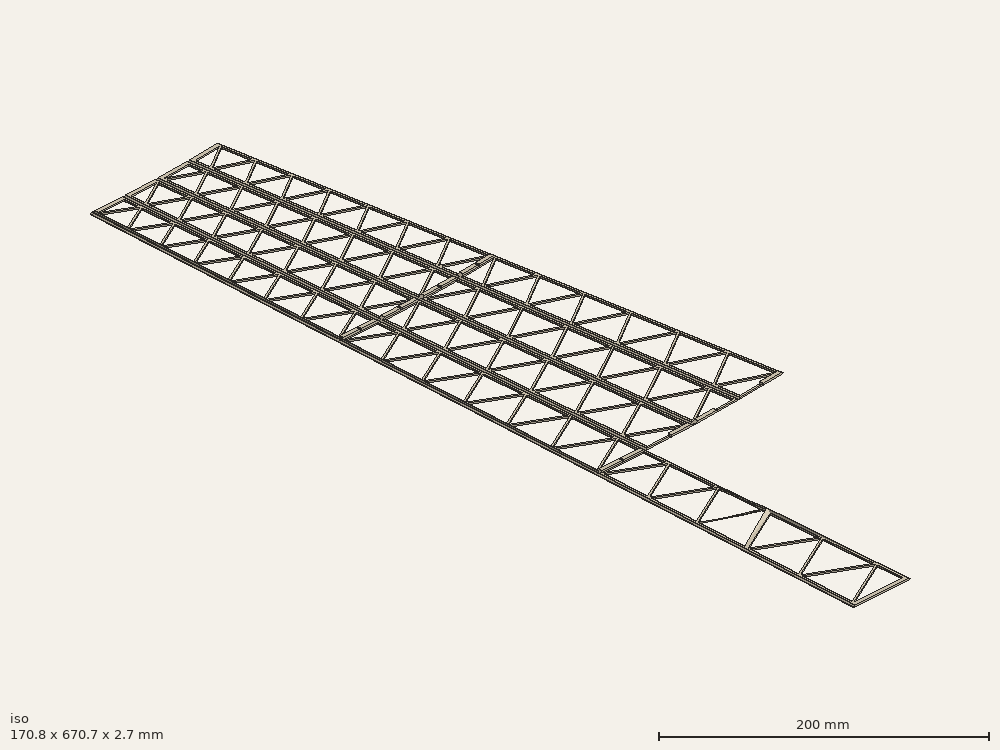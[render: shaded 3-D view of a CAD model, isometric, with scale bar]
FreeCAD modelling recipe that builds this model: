
FCSTD DOCUMENT  (FreeCAD 1.0R39319 (Git))
Label: DSB_30m_lystaarn_2
License: All rights reserved
LicenseURL: http://en.wikipedia.org/wiki/All_rights_reserved
objects: Sketcher::SketchObject×15, PartDesign::AdditivePipe×6, PartDesign::Body×4, PartDesign::Mirrored×4, PartDesign::SubShapeBinder×3, PartDesign::Pad×3, PartDesign::Chamfer×3, Image::ImagePlane×1, App::VarSet×1
note: 81 computed .brp shape members not serialized (recipe doc carries the construction recipe); baked Part::Feature solids carry a one-line shape summary decoded from their .brp

FEATURE [Image::ImagePlane] Taarn
  Placement = pos=(-63.4214,156.887,0) rot=(0,0,1;0.012217rad)
  XSize = 407.33
  YSize = 576.174
FEATURE [App::VarSet] VarSet
  IronLegWidth = 3
  IronSupportWidth = 1.5
  TowerBottomWidth = 45.5
  TowerHeight = 662.6
  TowerTopWidth = 25.97
  expr: TowerHeight = 353.87 + 308.73
FEATURE [Sketcher::SketchObject] Sketch  label="Basic Measurements"
  ArcFitTolerance = 1e-06
  AttachmentSupport = -> [XY_Plane]
  FullyConstrained = false
  MakeInternals = false
  MapMode = 5
  sketch-geometry (6):
    g0: LineSegment StartX=-22.75 StartY=0 StartZ=0 EndX=22.75 EndY=0 EndZ=0
    g1: LineSegment StartX=0 StartY=0 StartZ=0 EndX=0 EndY=353.87 EndZ=0
    g2: LineSegment StartX=-157.614 StartY=302.942 StartZ=0 EndX=-131.644 EndY=302.942 EndZ=0
    g3: LineSegment StartX=-144.629 StartY=302.942 StartZ=0 EndX=-143.643 EndY=-5.78841 EndZ=0
    g4: LineSegment StartX=-96.211 StartY=303.16 StartZ=0 EndX=-48.4821 EndY=303.16 EndZ=0
    g5: LineSegment StartX=-48.4821 StartY=327.388 StartZ=0 EndX=-48.4821 EndY=303.16 EndZ=0
  constraints (14):
    c: PointOnObject(g0,g-1)
    c: Coincident(g1,g-1)
    c: Vertical(g1)
    c: Symmetric(g0,g0,g1)
    c: DistanceX(g0,g0) = 45.5
    c: Horizontal(g2)
    c: DistanceX(g2,g2) = 25.97
    c: Symmetric(g2,g2,g3)
    c: DistanceY(g3,g3) = 308.73
    c: DistanceY(g1,g1) = 353.87
    c: Horizontal(g4)
    c: DistanceX(g4,g4) = 47.7289
    c: Coincident(g5,g4)
    c: DistanceY(g5,g5) = 24.2284
FEATURE [Sketcher::SketchObject] Sketch001  label="Basic Lattice Mast"
  ArcFitTolerance = 1e-06
  AttachmentSupport = -> [XY_Plane]
  FullyConstrained = true
  MakeInternals = false
  MapMode = 5
  expr: Constraints[128] = VarSet.IronSupportWidth
  expr: Constraints[56] = VarSet.IronSupportWidth * 2
  expr: Constraints[7] = VarSet.TowerTopWidth
  expr: Constraints[8] = VarSet.TowerBottomWidth
  expr: Constraints[91] = VarSet.IronSupportWidth * 2
  expr: Constraints[9] = VarSet.TowerHeight
  sketch-geometry (45):
    g0: LineSegment StartX=-22.75 StartY=0 StartZ=0 EndX=-12.985 EndY=662.6 EndZ=0
    g1: LineSegment StartX=-12.985 StartY=662.6 StartZ=0 EndX=12.985 EndY=662.6 EndZ=0
    g2: LineSegment StartX=12.985 StartY=662.6 StartZ=0 EndX=22.75 EndY=0 EndZ=0
    g3: LineSegment StartX=22.75 StartY=0 StartZ=0 EndX=-22.75 EndY=0 EndZ=0
    g4: LineSegment StartX=-22.7279 StartY=1.5 StartZ=0 EndX=22.3814 EndY=25.0125 EndZ=0
    g5: LineSegment StartX=22.3814 StartY=25.0125 StartZ=0 EndX=-22.0402 EndY=48.1665 EndZ=0
    g6: LineSegment StartX=-22.0402 StartY=48.1665 StartZ=0 EndX=21.7041 EndY=70.9675 EndZ=0
    g7: LineSegment StartX=21.7041 StartY=70.9675 StartZ=0 EndX=-21.3732 EndY=93.4209 EndZ=0
    g8: LineSegment [constr] StartX=22.3814 StartY=25.0125 StartZ=0 EndX=-22.3814 EndY=25.0125 EndZ=0
    g9: ArcOfCircle [constr] CenterX=22.3814 CenterY=25.0125 CenterZ=0 NormalX=0 NormalY=0 NormalZ=1 AngleXU=0 Radius=30 StartAngle=2.6611 EndAngle=3.62208
    g10: LineSegment [constr] StartX=-4.22167 StartY=38.8789 StartZ=0 EndX=-4.22167 EndY=11.1461 EndZ=0
    g11: LineSegment StartX=-21.3732 StartY=93.4209 StartZ=0 EndX=21.0474 EndY=115.532 EndZ=0
    g12: LineSegment StartX=21.0474 StartY=115.532 StartZ=0 EndX=-20.7265 EndY=137.306 EndZ=0
    g13: LineSegment StartX=-20.7265 StartY=137.306 StartZ=0 EndX=20.4105 EndY=158.748 EndZ=0
    g14: LineSegment StartX=20.4105 StartY=158.748 StartZ=0 EndX=-20.0993 EndY=179.863 EndZ=0
    g15: LineSegment StartX=-20.0993 StartY=179.863 StartZ=0 EndX=19.7929 EndY=200.656 EndZ=0
    g16: LineSegment StartX=19.7929 StartY=200.656 StartZ=0 EndX=-19.4911 EndY=221.132 EndZ=0
    g17: LineSegment StartX=-19.4469 StartY=224.132 StartZ=0 EndX=19.1504 EndY=244.25 EndZ=0
    g18: LineSegment StartX=19.1504 StartY=244.25 StartZ=0 EndX=-18.8584 EndY=264.062 EndZ=0
    g19: LineSegment StartX=-18.8584 StartY=264.062 StartZ=0 EndX=18.5709 EndY=283.571 EndZ=0
    g20: LineSegment StartX=18.5709 StartY=283.571 StartZ=0 EndX=-18.2878 EndY=302.783 EndZ=0
    g21: LineSegment StartX=-18.2878 StartY=302.783 StartZ=0 EndX=18.0089 EndY=321.702 EndZ=0
    g22: LineSegment StartX=18.0089 StartY=321.702 StartZ=0 EndX=-17.7344 EndY=340.333 EndZ=0
    g23: LineSegment StartX=-17.7344 StartY=340.333 StartZ=0 EndX=17.464 EndY=358.68 EndZ=0
    g24: LineSegment StartX=17.464 StartY=358.68 StartZ=0 EndX=-17.1977 EndY=376.747 EndZ=0
    g25: LineSegment StartX=-17.1977 StartY=376.747 StartZ=0 EndX=16.9355 EndY=394.538 EndZ=0
    g26: LineSegment StartX=16.9355 StartY=394.538 StartZ=0 EndX=-16.6773 EndY=412.058 EndZ=0
    g27: LineSegment StartX=-16.6773 StartY=412.058 StartZ=0 EndX=16.4231 EndY=429.311 EndZ=0
    g28: LineSegment StartX=16.4231 StartY=429.311 StartZ=0 EndX=-16.1727 EndY=446.301 EndZ=0
    g29: LineSegment StartX=-16.1285 StartY=449.301 StartZ=0 EndX=15.8826 EndY=465.987 EndZ=0
    g30: LineSegment StartX=15.8826 StartY=465.987 StartZ=0 EndX=-15.6404 EndY=482.417 EndZ=0
    g31: LineSegment StartX=-15.6404 StartY=482.417 StartZ=0 EndX=15.402 EndY=498.598 EndZ=0
    g32: LineSegment StartX=15.402 StartY=498.598 StartZ=0 EndX=-15.1671 EndY=514.531 EndZ=0
    g33: LineSegment StartX=-15.1671 StartY=514.531 StartZ=0 EndX=14.9359 EndY=530.222 EndZ=0
    g34: LineSegment StartX=14.9359 StartY=530.222 StartZ=0 EndX=-14.7082 EndY=545.674 EndZ=0
    g35: LineSegment StartX=-14.7082 StartY=545.674 StartZ=0 EndX=14.4839 EndY=560.89 EndZ=0
    g36: LineSegment StartX=14.4839 StartY=560.89 StartZ=0 EndX=-14.2631 EndY=575.874 EndZ=0
    g37: LineSegment StartX=-14.2631 StartY=575.874 StartZ=0 EndX=14.0457 EndY=590.629 EndZ=0
    g38: LineSegment StartX=14.0457 StartY=590.629 StartZ=0 EndX=-13.8315 EndY=605.16 EndZ=0
    g39: LineSegment StartX=-13.8315 StartY=605.16 StartZ=0 EndX=13.6206 EndY=619.469 EndZ=0
    g40: LineSegment StartX=13.6206 StartY=619.469 StartZ=0 EndX=-13.413 EndY=633.56 EndZ=0
    g41: LineSegment StartX=-13.413 StartY=633.56 StartZ=0 EndX=13.2085 EndY=647.436 EndZ=0
    g42: LineSegment StartX=13.2085 StartY=647.436 StartZ=0 EndX=-13.0071 EndY=661.1 EndZ=0
    g43: LineSegment StartX=-16.1506 StartY=447.801 StartZ=0 EndX=16.1506 EndY=447.801 EndZ=0
    g44: LineSegment StartX=-19.469 StartY=222.632 StartZ=0 EndX=19.469 EndY=222.632 EndZ=0
  constraints (136):
    c: Coincident(g0,g1)
    c: Coincident(g1,g2)
    c: Coincident(g2,g3)
    c: Coincident(g3,g0)
    c: Horizontal(g3)
    c: Symmetric(g0,g2,g-1)
    c: Symmetric(g1,g0,g-2)
    c: DistanceX(g1,g1) = 25.97
    c: DistanceX(g3,g3) = 45.5
    c: DistanceY(g-1,g1) = 662.6
    c: Coincident(g4,g5)
    c: Coincident(g5,g6)
    c: Coincident(g6,g7)
    c: Coincident(g8,g4)
    c: PointOnObject(g8,g0)
    c: Horizontal(g8)
    c: Coincident(g9,g4)
    c: PointOnObject(g9,g5)
    c: PointOnObject(g9,g4)
    c: Coincident(g10,g9)
    c: Coincident(g10,g9)
    c: Vertical(g10)
    c: Parallel(g4,g6)
    c: Parallel(g7,g5)
    c: PointOnObject(g7,g0)
    c: PointOnObject(g5,g0)
    c: PointOnObject(g4,g0)
    c: PointOnObject(g6,g2)
    c: PointOnObject(g4,g2) = 1.5
    c: DistanceY(g0,g4) = 1.5
    c: Coincident(g11,g12)
    c: Coincident(g12,g13)
    c: Coincident(g13,g14)
    c: Parallel(g6,g11)
    c: Parallel(g11,g13)
    c: Parallel(g14,g12)
    c: Parallel(g12,g7)
    c: Coincident(g11,g7)
    c: PointOnObject(g12,g0)
    c: PointOnObject(g14,g0)
    c: PointOnObject(g13,g2)
    c: PointOnObject(g11,g2)
    c: Coincident(g14,g15)
    c: Coincident(g15,g16)
    c: Parallel(g14,g16)
    c: Parallel(g15,g13)
    c: PointOnObject(g16,g0)
    c: PointOnObject(g15,g2)
    c: Coincident(g17,g18)
    c: Coincident(g18,g19)
    c: Coincident(g19,g20)
    c: Parallel(g20,g18)
    c: Parallel(g18,g16)
    c: Parallel(g15,g17)
    c: Parallel(g17,g19)
    c: PointOnObject(g17,g0)
    c: DistanceY(g16,g17) = 3
    c: PointOnObject(g18,g0)
    c: PointOnObject(g17,g2)
    c: PointOnObject(g19,g2)
    c: PointOnObject(g20,g0)
    c: Coincident(g21,g22)
    c: Coincident(g22,g23)
    c: Parallel(g19,g21)
    c: Parallel(g21,g23)
    c: Parallel(g20,g22)
    c: Coincident(g21,g20)
    c: PointOnObject(g22,g0)
    c: PointOnObject(g21,g2)
    c: PointOnObject(g23,g2)
    c: Coincident(g24,g25)
    c: Coincident(g25,g26)
    c: Coincident(g26,g27)
    c: Coincident(g27,g28)
    c: Parallel(g27,g25)
    c: Parallel(g25,g23)
    c: Parallel(g28,g26)
    c: Parallel(g26,g22)
    c: Coincident(g24,g23)
    c: PointOnObject(g24,g0)
    c: PointOnObject(g25,g2)
    c: Parallel(g24,g22)
    c: PointOnObject(g26,g0)
    c: PointOnObject(g27,g2)
    c: PointOnObject(g28,g0)
    c: Coincident(g29,g30)
    c: Parallel(g27,g29)
    c: Parallel(g30,g28)
    c: PointOnObject(g29,g0)
    c: PointOnObject(g30,g0)
    c: PointOnObject(g29,g2)
    c: DistanceY(g28,g29) = 3
    c: Coincident(g31,g32)
    c: Coincident(g33,g34)
    c: Coincident(g35,g36)
    c: Parallel(g32,g34)
    c: Parallel(g34,g36)
    c: Parallel(g36,g30)
    c: Parallel(g29,g31)
    c: Parallel(g31,g33)
    c: Parallel(g33,g35)
    c: Coincident(g32,g33)
    c: Coincident(g31,g30)
    c: PointOnObject(g31,g2)
    c: PointOnObject(g32,g0)
    c: PointOnObject(g33,g2)
    c: PointOnObject(g34,g0)
    c: Coincident(g35,g34)
    c: PointOnObject(g35,g2)
    c: PointOnObject(g36,g0)
    c: Coincident(g37,g38)
    c: Coincident(g39,g40)
    c: Parallel(g35,g37)
    c: Parallel(g37,g39)
    c: Parallel(g40,g38)
    c: Parallel(g38,g36)
    c: Coincident(g37,g36)
    c: PointOnObject(g37,g2)
    c: PointOnObject(g38,g0)
    c: Coincident(g39,g38)
    c: PointOnObject(g40,g0)
    c: PointOnObject(g39,g2)
    c: Coincident(g40,g41)
    c: Coincident(g41,g42)
    c: Parallel(g40,g42)
    c: Parallel(g41,g39)
    c: PointOnObject(g41,g2)
    c: PointOnObject(g42,g0)
    c: DistanceY(g42,g0) = 1.5
    c: Radius(g9) = 30
    c: Horizontal(g43)
    c: PointOnObject(g43,g2)
    c: Symmetric(g28,g29,g43)
    c: Horizontal(g44)
    c: PointOnObject(g44,g2)
    c: Symmetric(g16,g17,g44)
FEATURE [PartDesign::Body] Body
  AllowCompound = true
  Group = -> [Sketch,Sketch001]
  Origin = -> Origin
FEATURE [PartDesign::SubShapeBinder] Binder
  BindCopyOnChange = 0
  BindMode = 0
  ClaimChildren = false
  Context = -> Body001 [Binder.]
  Fuse = false
  MakeFace = true
  OffsetFill = false
  OffsetIntersection = false
  OffsetJoinType = 0
  OffsetOpenResult = false
  PartialLoad = false
  Refine = true
  Relative = true
  Support = -> [Body[Sketch001.]]
  _Version = 2
FEATURE [Sketcher::SketchObject] Sketch002
  ArcFitTolerance = 1e-06
  AttachmentSupport = -> [XY_Plane001]
  ExternalGeometry = -> [Binder]
  FullyConstrained = true
  MakeInternals = false
  MapMode = 5
  expr: Constraints[11] = VarSet.IronLegWidth / 2
  expr: Constraints[33] = VarSet.IronLegWidth
  sketch-geometry (52):
    g0: LineSegment StartX=-17.6509 StartY=447.801 StartZ=0 EndX=-14.4632 EndY=664.1 EndZ=0
    g1: LineSegment StartX=-14.4632 StartY=664.1 StartZ=0 EndX=14.4632 EndY=664.1 EndZ=0
    g2: LineSegment StartX=14.4632 StartY=664.1 StartZ=0 EndX=17.6509 EndY=447.801 EndZ=0
    g3: LineSegment StartX=-17.6509 StartY=447.801 StartZ=0 EndX=17.6509 EndY=447.801 EndZ=0
    g4: LineSegment [constr] StartX=-12.985 StartY=662.6 StartZ=0 EndX=-14.485 EndY=662.622 EndZ=0
    g5: LineSegment [constr] StartX=-12.985 StartY=662.6 StartZ=0 EndX=-12.985 EndY=664.1 EndZ=0
    g6: LineSegment StartX=11.5068 StartY=661.1 StartZ=0 EndX=-11.5068 EndY=661.1 EndZ=0
    g7: LineSegment StartX=-11.5068 StartY=661.1 StartZ=0 EndX=11.6849 EndY=649.012 EndZ=0
    g8: LineSegment StartX=11.6849 StartY=649.012 StartZ=0 EndX=11.5068 EndY=661.1 EndZ=0
    g9: LineSegment StartX=-11.5297 StartY=659.548 StartZ=0 EndX=11.7082 EndY=647.436 EndZ=0
    g10: LineSegment StartX=11.7082 StartY=647.436 StartZ=0 EndX=-11.8894 EndY=635.136 EndZ=0
    g11: LineSegment StartX=-11.8894 StartY=635.136 StartZ=0 EndX=-11.5297 EndY=659.548 EndZ=0
    g12: LineSegment [constr] StartX=-11.5297 StartY=659.548 StartZ=0 EndX=-14.5297 EndY=659.592 EndZ=0
    g13: LineSegment StartX=11.731 StartY=645.883 StartZ=0 EndX=-11.9127 EndY=633.56 EndZ=0
    g14: LineSegment StartX=-11.9127 StartY=633.56 StartZ=0 EndX=12.0971 EndY=621.045 EndZ=0
    g15: LineSegment StartX=12.0971 StartY=621.045 StartZ=0 EndX=11.731 EndY=645.883 EndZ=0
    g16: LineSegment StartX=-11.9355 StartY=632.007 StartZ=0 EndX=12.1203 EndY=619.469 EndZ=0
    g17: LineSegment StartX=12.1203 StartY=619.469 StartZ=0 EndX=-12.308 EndY=606.736 EndZ=0
    g18: LineSegment StartX=-12.308 StartY=606.736 StartZ=0 EndX=-11.9355 EndY=632.007 EndZ=0
    g19: LineSegment StartX=12.1432 StartY=617.917 StartZ=0 EndX=-12.3312 EndY=605.16 EndZ=0
    g20: LineSegment StartX=-12.3312 StartY=605.16 StartZ=0 EndX=12.5221 EndY=592.205 EndZ=0
    g21: LineSegment StartX=12.5221 StartY=592.205 StartZ=0 EndX=12.1432 EndY=617.917 EndZ=0
    g22: LineSegment StartX=-12.3541 StartY=603.608 StartZ=0 EndX=12.5453 EndY=590.629 EndZ=0
    g23: LineSegment StartX=12.5453 StartY=590.629 StartZ=0 EndX=-12.7396 EndY=577.45 EndZ=0
    g24: LineSegment StartX=-12.7396 StartY=577.45 StartZ=0 EndX=-12.3541 EndY=603.608 EndZ=0
    g25: LineSegment StartX=12.5682 StartY=589.077 StartZ=0 EndX=-12.7628 EndY=575.874 EndZ=0
    g26: LineSegment StartX=-12.7628 StartY=575.874 StartZ=0 EndX=12.9604 EndY=562.466 EndZ=0
    g27: LineSegment StartX=12.9604 StartY=562.466 StartZ=0 EndX=12.5682 EndY=589.077 EndZ=0
    g28: LineSegment StartX=-12.7857 StartY=574.321 StartZ=0 EndX=12.9836 EndY=560.89 EndZ=0
    g29: LineSegment StartX=12.9836 StartY=560.89 StartZ=0 EndX=-13.1846 EndY=547.25 EndZ=0
    g30: LineSegment StartX=-13.1846 StartY=547.25 StartZ=0 EndX=-12.7857 EndY=574.321 EndZ=0
    g31: LineSegment StartX=-13.2079 StartY=545.674 StartZ=0 EndX=13.0065 EndY=559.338 EndZ=0
    g32: LineSegment StartX=13.0065 StartY=559.338 StartZ=0 EndX=13.4124 EndY=531.798 EndZ=0
    g33: LineSegment StartX=13.4124 StartY=531.798 StartZ=0 EndX=-13.2079 EndY=545.674 EndZ=0
    g34: LineSegment StartX=-13.2307 StartY=544.122 StartZ=0 EndX=-13.6436 EndY=516.108 EndZ=0
    g35: LineSegment StartX=-13.6436 StartY=516.108 StartZ=0 EndX=13.4356 EndY=530.222 EndZ=0
    g36: LineSegment StartX=13.4356 StartY=530.222 StartZ=0 EndX=-13.2307 EndY=544.122 EndZ=0
    g37: LineSegment StartX=13.4585 StartY=528.67 StartZ=0 EndX=-13.6668 EndY=514.531 EndZ=0
    g38: LineSegment StartX=-13.6668 StartY=514.531 StartZ=0 EndX=13.8784 EndY=500.174 EndZ=0
    g39: LineSegment StartX=13.8784 StartY=500.174 StartZ=0 EndX=13.4585 EndY=528.67 EndZ=0
    g40: LineSegment StartX=-13.6897 StartY=512.979 StartZ=0 EndX=13.9016 EndY=498.598 EndZ=0
    g41: LineSegment StartX=13.9016 StartY=498.598 StartZ=0 EndX=-14.1169 EndY=483.994 EndZ=0
    g42: LineSegment StartX=-14.1169 StartY=483.994 StartZ=0 EndX=-13.6897 EndY=512.979 EndZ=0
    g43: LineSegment StartX=13.9245 StartY=497.046 StartZ=0 EndX=-14.1401 EndY=482.417 EndZ=0
    g44: LineSegment StartX=-14.1401 StartY=482.417 StartZ=0 EndX=14.359 EndY=467.563 EndZ=0
    g45: LineSegment StartX=14.359 StartY=467.563 StartZ=0 EndX=13.9245 EndY=497.046 EndZ=0
    g46: LineSegment StartX=-14.163 StartY=480.865 StartZ=0 EndX=14.3822 EndY=465.987 EndZ=0
    g47: LineSegment StartX=14.3822 StartY=465.987 StartZ=0 EndX=-14.6049 EndY=450.877 EndZ=0
    g48: LineSegment StartX=-14.6049 StartY=450.877 StartZ=0 EndX=-14.163 EndY=480.865 EndZ=0
    g49: LineSegment StartX=-14.6281 StartY=449.301 StartZ=0 EndX=14.4051 EndY=464.434 EndZ=0
    g50: LineSegment StartX=14.4051 StartY=464.434 StartZ=0 EndX=14.6281 EndY=449.301 EndZ=0
    g51: LineSegment StartX=14.6281 StartY=449.301 StartZ=0 EndX=-14.6281 EndY=449.301 EndZ=0
  constraints (154):
    c: Coincident(g0,g1)
    c: Coincident(g1,g2)
    c: Coincident(g3,g0)
    c: Coincident(g3,g2)
    c: Horizontal(g3)
    c: Parallel(g0,g-8)
    c: Parallel(g2,g-7)
    c: Symmetric(g1,g0,g-2)
    c: Coincident(g4,g-8)
    c: PointOnObject(g4,g0)
    c: Perpendicular(g0,g4)
    c: DistanceX(g4,g4) = 1.5
    c: Coincident(g5,g4)
    c: PointOnObject(g5,g1)
    c: Perpendicular(g5,g1)
    c: Equal(g5,g4)
    c: Coincident(g6,g7)
    c: Coincident(g7,g8)
    c: Coincident(g8,g6)
    c: Coincident(g9,g10)
    c: Coincident(g10,g11)
    c: Coincident(g11,g9)
    c: Parallel(g9,g7)
    c: Parallel(g7,g-3)
    c: Parallel(g11,g-8)
    c: Parallel(g10,g-4)
    c: Horizontal(g9,g-4)
    c: Parallel(g8,g-7)
    c: Horizontal(g6,g-3)
    c: PointOnObject(g6,g11)
    c: Coincident(g12,g9)
    c: PointOnObject(g12,g0)
    c: Perpendicular(g0,g12)
    c: DistanceX(g12,g12) = 3
    c: Symmetric(g6,g6,g-2)
    c: PointOnObject(g9,g8)
    c: Coincident(g13,g14)
    c: Coincident(g14,g15)
    c: Coincident(g15,g13)
    c: Coincident(g16,g17)
    c: Coincident(g17,g18)
    c: Coincident(g18,g16)
    c: Parallel(g18,g-8)
    c: Parallel(g15,g-7)
    c: Horizontal(g13,g-6)
    c: Horizontal(g16,g-9)
    c: PointOnObject(g16,g15)
    c: PointOnObject(g13,g18)
    c: PointOnObject(g13,g11)
    c: PointOnObject(g13,g8)
    c: Parallel(g13,g-4)
    c: Parallel(g14,g-6)
    c: Parallel(g16,g-6)
    c: Parallel(g17,g-9)
    c: Coincident(g19,g20)
    c: Coincident(g20,g21)
    c: Coincident(g21,g19)
    c: Coincident(g22,g23)
    c: Coincident(g23,g24)
    c: Coincident(g24,g22)
    c: Coincident(g25,g26)
    c: Coincident(g26,g27)
    c: Coincident(g27,g25)
    c: Horizontal(g19,g-10)
    c: Horizontal(g22,g-11)
    c: Horizontal(g25,g-12)
    c: Parallel(g19,g-9)
    c: Parallel(g21,g-7)
    c: Parallel(g20,g-10)
    c: Parallel(g-10,g22)
    c: Parallel(g24,g-8)
    c: Parallel(g23,g-11)
    c: Parallel(g25,g-11)
    c: Parallel(g27,g-7)
    c: Parallel(g26,g-12)
    c: PointOnObject(g19,g18)
    c: PointOnObject(g22,g18)
    c: PointOnObject(g25,g24)
    c: PointOnObject(g19,g15)
    c: PointOnObject(g22,g21)
    c: PointOnObject(g25,g21)
    c: Coincident(g28,g29)
    c: Coincident(g29,g30)
    c: Coincident(g30,g28)
    c: Coincident(g31,g32)
    c: Coincident(g32,g33)
    c: Coincident(g33,g31)
    c: Coincident(g34,g35)
    c: Coincident(g35,g36)
    c: Coincident(g36,g34)
    c: Coincident(g37,g38)
    c: Coincident(g38,g39)
    c: Coincident(g39,g37)
    c: Horizontal(g28,g-13)
    c: Horizontal(g31,g-14)
    c: Horizontal(g35,g-15)
    c: Horizontal(g37,g-16)
    c: Parallel(g30,g34)
    c: Parallel(g34,g-8)
    c: Parallel(g32,g39)
    c: Parallel(g39,g-7)
    c: Parallel(g31,g-13)
    c: Parallel(g-13,g29)
    c: Parallel(g28,g-12)
    c: Parallel(g33,g-14)
    c: Parallel(g-14,g36)
    c: Parallel(g37,g35)
    c: Parallel(g35,g-15)
    c: Parallel(g38,g-16)
    c: PointOnObject(g28,g27)
    c: PointOnObject(g31,g27)
    c: PointOnObject(g35,g32)
    c: PointOnObject(g37,g32)
    c: PointOnObject(g28,g24)
    c: PointOnObject(g31,g30)
    c: PointOnObject(g34,g30)
    c: PointOnObject(g37,g34)
    c: Coincident(g40,g41)
    c: Coincident(g41,g42)
    c: Coincident(g42,g40)
    c: Coincident(g43,g44)
    c: Coincident(g44,g45)
    c: Coincident(g45,g43)
    c: Coincident(g46,g47)
    c: Coincident(g47,g48)
    c: Coincident(g48,g46)
    c: Coincident(g49,g50)
    c: Coincident(g50,g51)
    c: Coincident(g51,g49)
    c: Horizontal(g51)
    c: Parallel(g40,g-16)
    c: Parallel(g41,g-17)
    c: Parallel(g42,g-8)
    c: Parallel(g43,g-17)
    c: Parallel(g44,g-18)
    c: Parallel(g45,g-7)
    c: Parallel(g46,g-18)
    c: Parallel(g47,g-19)
    c: Parallel(g48,g-8)
    c: Parallel(g49,g-19)
    c: Parallel(g50,g-7)
    c: Horizontal(g40,g-17)
    c: Horizontal(g43,g-18)
    c: Horizontal(g46,g-19)
    c: Horizontal(g49,g-19)
    c: PointOnObject(g40,g34)
    c: PointOnObject(g40,g39)
    c: PointOnObject(g43,g39)
    c: PointOnObject(g43,g42)
    c: PointOnObject(g46,g42)
    c: PointOnObject(g46,g45)
    c: PointOnObject(g49,g48)
    c: PointOnObject(g49,g45)
    c: Horizontal(g0,g-20)
FEATURE [PartDesign::Pad] Pad
  Direction = (0,0,1)
  Length = 1.2
  Length2 = 10
  Profile = -> Sketch002
  ReferenceAxis = -> Sketch002 [N_Axis]
  Refine = true
  Suppressed = false
  Type = 0
FEATURE [PartDesign::Chamfer] Chamfer
  Angle = 50
  Base = -> Pad [Edge4,Edge10]
  BaseFeature = -> Pad
  ChamferType = 2
  FlipDirection = false
  Refine = true
  Size = 1
  Size2 = 1
  SupportTransform = false
  Suppressed = false
  UseAllEdges = false
FEATURE [Sketcher::SketchObject] Sketch003
  ArcFitTolerance = 1e-06
  AttachmentSupport = -> [Chamfer]
  ExternalGeometry = -> [Chamfer]
  FullyConstrained = true
  MakeInternals = false
  MapMode = 5
  Placement = pos=(0,447.801,0) rot=(1,0,0;1.5708rad)
  sketch-geometry (4):
    g0: LineSegment StartX=-16.459 StartY=1.2 StartZ=0 EndX=-14.6712 EndY=2.7 EndZ=0
    g1: LineSegment StartX=-14.6712 StartY=2.7 StartZ=0 EndX=-0.5 EndY=2.7 EndZ=0
    g2: LineSegment StartX=-0.5 StartY=2.7 StartZ=0 EndX=-0.5 EndY=1.2 EndZ=0
    g3: LineSegment StartX=-0.5 StartY=1.2 StartZ=0 EndX=-16.459 EndY=1.2 EndZ=0
  constraints (11):
    c: Coincident(g0,g1)
    c: Horizontal(g1)
    c: Coincident(g1,g2)
    c: Coincident(g2,g3)
    c: Coincident(g3,g0)
    c: Horizontal(g3)
    c: Vertical(g2)
    c: Parallel(g0,g-3)
    c: Coincident(g0,g-3)
    c: DistanceX(g2,g-1) = 0.5
    c: DistanceY(g2,g2) = 1.5
FEATURE [Sketcher::SketchObject] Sketch004
  ArcFitTolerance = 1e-06
  AttachmentSupport = -> [Chamfer]
  ExternalGeometry = -> [Chamfer]
  FullyConstrained = true
  MakeInternals = false
  MapMode = 5
  Placement = pos=(0,0,1.2) rot=(0,0,1;0rad)
  sketch-geometry (1):
    g0: LineSegment StartX=-16.4369 StartY=449.301 StartZ=0 EndX=-16.4811 EndY=446.301 EndZ=0
  constraints (4):
    c: Parallel(g-3,g0)
    c: Horizontal(g0,g-4)
    c: DistanceY(g0,g-3) = 1.5
    c: PointOnObject(g0,g-3)
FEATURE [PartDesign::AdditivePipe] AdditivePipe
  AuxilleryCurvelinear = true
  AuxillerySpineTangent = false
  BaseFeature = -> Chamfer
  Binormal = (0,0,0)
  Mode = 0
  Profile = -> Sketch003
  Refine = true
  Spine = -> Sketch004
  SpineTangent = false
  Suppressed = false
  Transformation = 0
  Transition = 0
FEATURE [PartDesign::Mirrored] Mirrored
  BaseFeature = -> AdditivePipe
  MirrorPlane = -> AdditivePipe [Face55]
  Originals = -> [AdditivePipe]
  Refine = true
  Suppressed = false
  TransformMode = 1
FEATURE [PartDesign::Mirrored] Mirrored001
  BaseFeature = -> Mirrored
  MirrorPlane = -> Mirrored [Face59]
  Originals = -> [Mirrored]
  Refine = true
  Suppressed = false
  TransformMode = 1
FEATURE [Sketcher::SketchObject] Sketch005
  ArcFitTolerance = 1e-06
  AttachmentSupport = -> [Mirrored001]
  ExternalGeometry = -> [Mirrored001]
  FullyConstrained = true
  MakeInternals = false
  MapMode = 5
  Placement = pos=(0,447.801,0) rot=(1,0,0;1.5708rad)
  sketch-geometry (3):
    g0: LineSegment StartX=-15.9369 StartY=1.2 StartZ=0 EndX=-15.9369 EndY=2.7 EndZ=0
    g1: LineSegment StartX=-15.9369 StartY=2.7 StartZ=0 EndX=-14.6049 EndY=1.2 EndZ=0
    g2: LineSegment StartX=-14.6049 StartY=1.2 StartZ=0 EndX=-15.9369 EndY=1.2 EndZ=0
  constraints (8):
    c: Vertical(g0)
    c: Coincident(g0,g1)
    c: Coincident(g1,g2)
    c: Coincident(g2,g0)
    c: Parallel(g2,g-3)
    c: Distance(g0,g-3) = 0.5
    c: Coincident(g1,g-5)
    c: DistanceY(g0,g0) = 1.5
FEATURE [PartDesign::AdditivePipe] AdditivePipe001
  AuxilleryCurvelinear = true
  AuxillerySpineTangent = false
  BaseFeature = -> Mirrored001
  Binormal = (0,0,0)
  Mode = 0
  Profile = -> Sketch005
  Refine = true
  Spine = -> Mirrored001 [Edge74]
  SpineTangent = false
  Suppressed = false
  Transformation = 0
  Transition = 0
FEATURE [PartDesign::Body] Body001  label="TowerTopSection"
  AllowCompound = true
  Group = -> [Binder,Sketch002,Pad,Chamfer,Sketch003,Sketch004,AdditivePipe,Mirrored,Mirrored001,Sketch005,AdditivePipe001]
  Origin = -> Origin001
  Tip = -> AdditivePipe001
FEATURE [PartDesign::SubShapeBinder] Binder001
  BindCopyOnChange = 0
  BindMode = 0
  ClaimChildren = false
  Context = -> Body002 [Binder001.]
  Fuse = false
  MakeFace = true
  OffsetFill = false
  OffsetIntersection = false
  OffsetJoinType = 0
  OffsetOpenResult = false
  PartialLoad = false
  Refine = true
  Relative = true
  Support = -> [Body[Sketch001.]]
  _Version = 2
FEATURE [Sketcher::SketchObject] Sketch006
  ArcFitTolerance = 1e-06
  AttachmentSupport = -> [XY_Plane002]
  ExternalGeometry = -> [Binder001]
  FullyConstrained = true
  MakeInternals = false
  MapMode = 5
  expr: Constraints[10] = VarSet.IronLegWidth / 2
  expr: Constraints[31] = VarSet.IronLegWidth
  sketch-geometry (46):
    g0: LineSegment StartX=-20.9693 StartY=222.632 StartZ=0 EndX=-17.6509 EndY=447.801 EndZ=0
    g1: LineSegment StartX=-17.6509 StartY=447.801 StartZ=0 EndX=17.6509 EndY=447.801 EndZ=0
    g2: LineSegment StartX=17.6509 StartY=447.801 StartZ=0 EndX=20.9693 EndY=222.632 EndZ=0
    g3: LineSegment StartX=20.9693 StartY=222.632 StartZ=0 EndX=-20.9693 EndY=222.632 EndZ=0
    g4: LineSegment [constr] StartX=-16.1727 StartY=446.301 StartZ=0 EndX=-17.6727 EndY=446.323 EndZ=0
    g5: LineSegment StartX=-14.6727 StartY=446.301 StartZ=0 EndX=14.6727 EndY=446.301 EndZ=0
    g6: LineSegment StartX=14.6727 StartY=446.301 StartZ=0 EndX=14.8998 EndY=430.887 EndZ=0
    g7: LineSegment StartX=14.8998 StartY=430.887 StartZ=0 EndX=-14.6727 EndY=446.301 EndZ=0
    g8: LineSegment StartX=-14.6955 StartY=444.75 StartZ=0 EndX=14.9231 EndY=429.311 EndZ=0
    g9: LineSegment StartX=14.9231 StartY=429.311 StartZ=0 EndX=-15.1541 EndY=413.634 EndZ=0
    g10: LineSegment StartX=-15.1541 StartY=413.634 StartZ=0 EndX=-14.6955 EndY=444.75 EndZ=0
    g11: LineSegment StartX=-15.1773 StartY=412.058 StartZ=0 EndX=14.9459 EndY=427.76 EndZ=0
    g12: LineSegment StartX=14.9459 StartY=427.76 StartZ=0 EndX=15.4123 EndY=396.114 EndZ=0
    g13: LineSegment StartX=15.4123 StartY=396.114 StartZ=0 EndX=-15.1773 EndY=412.058 EndZ=0
    g14: LineSegment StartX=-15.2002 StartY=410.506 StartZ=0 EndX=15.4355 EndY=394.538 EndZ=0
    g15: LineSegment StartX=15.4355 StartY=394.538 StartZ=0 EndX=-15.6745 EndY=378.322 EndZ=0
    g16: LineSegment StartX=-15.6745 StartY=378.322 StartZ=0 EndX=-15.2002 EndY=410.506 EndZ=0
    g17: LineSegment [constr] StartX=14.6727 StartY=446.301 StartZ=0 EndX=17.6724 EndY=446.346 EndZ=0
    g18: LineSegment [constr] StartX=-14.6955 StartY=444.75 StartZ=0 EndX=-17.6952 EndY=444.794 EndZ=0
    g19: LineSegment StartX=-15.6977 StartY=376.747 StartZ=0 EndX=15.4584 EndY=392.986 EndZ=0
    g20: LineSegment StartX=15.4584 StartY=392.986 StartZ=0 EndX=15.9408 EndY=360.256 EndZ=0
    g21: LineSegment StartX=15.9408 StartY=360.256 StartZ=0 EndX=-15.6977 EndY=376.747 EndZ=0
    g22: LineSegment StartX=-15.7206 StartY=375.195 StartZ=0 EndX=15.964 EndY=358.68 EndZ=0
    g23: LineSegment StartX=15.964 StartY=358.68 StartZ=0 EndX=-16.2112 EndY=341.909 EndZ=0
    g24: LineSegment StartX=-16.2112 StartY=341.909 StartZ=0 EndX=-15.7206 EndY=375.195 EndZ=0
    g25: LineSegment StartX=-16.2344 StartY=340.333 StartZ=0 EndX=15.9869 EndY=357.128 EndZ=0
    g26: LineSegment StartX=15.9869 StartY=357.128 StartZ=0 EndX=16.4857 EndY=323.278 EndZ=0
    g27: LineSegment StartX=16.4857 StartY=323.278 StartZ=0 EndX=-16.2344 EndY=340.333 EndZ=0
    g28: LineSegment StartX=-16.2572 StartY=338.781 StartZ=0 EndX=-16.7645 EndY=304.359 EndZ=0
    g29: LineSegment StartX=-16.7645 StartY=304.359 StartZ=0 EndX=16.5089 EndY=321.702 EndZ=0
    g30: LineSegment StartX=16.5089 StartY=321.702 StartZ=0 EndX=-16.2572 EndY=338.781 EndZ=0
    g31: LineSegment StartX=-16.7878 StartY=302.783 StartZ=0 EndX=16.5318 EndY=320.151 EndZ=0
    g32: LineSegment StartX=16.5318 StartY=320.151 StartZ=0 EndX=17.0477 EndY=285.147 EndZ=0
    g33: LineSegment StartX=17.0477 StartY=285.147 StartZ=0 EndX=-16.7878 EndY=302.783 EndZ=0
    g34: LineSegment StartX=-16.8106 StartY=301.232 StartZ=0 EndX=17.0709 EndY=283.571 EndZ=0
    g35: LineSegment StartX=17.0709 StartY=283.571 StartZ=0 EndX=-17.3352 EndY=265.638 EndZ=0
    g36: LineSegment StartX=-17.3352 StartY=265.638 StartZ=0 EndX=-16.8106 EndY=301.232 EndZ=0
    g37: LineSegment StartX=-17.3584 StartY=264.062 StartZ=0 EndX=17.0938 EndY=282.02 EndZ=0
    g38: LineSegment StartX=17.0938 StartY=282.02 StartZ=0 EndX=17.6272 EndY=245.826 EndZ=0
    g39: LineSegment StartX=17.6272 StartY=245.826 StartZ=0 EndX=-17.3584 EndY=264.062 EndZ=0
    g40: LineSegment StartX=-17.3813 StartY=262.51 StartZ=0 EndX=-17.9237 EndY=225.708 EndZ=0
    g41: LineSegment StartX=-17.9237 StartY=225.708 StartZ=0 EndX=17.6504 EndY=244.25 EndZ=0
    g42: LineSegment StartX=17.6504 StartY=244.25 StartZ=0 EndX=-17.3813 EndY=262.51 EndZ=0
    g43: LineSegment StartX=-17.9469 StartY=224.132 StartZ=0 EndX=17.6733 EndY=242.699 EndZ=0
    g44: LineSegment StartX=17.6733 StartY=242.699 StartZ=0 EndX=17.9469 EndY=224.132 EndZ=0
    g45: LineSegment StartX=17.9469 StartY=224.132 StartZ=0 EndX=-17.9469 EndY=224.132 EndZ=0
  constraints (137):
    c: Coincident(g0,g1)
    c: Coincident(g1,g2)
    c: Coincident(g2,g3)
    c: Horizontal(g3)
    c: Coincident(g0,g3)
    c: Parallel(g-3,g0)
    c: Parallel(g-4,g2)
    c: Symmetric(g1,g0,g-2)
    c: PointOnObject(g4,g0)
    c: Perpendicular(g4,g0)
    c: DistanceX(g4,g4) = 1.5
    c: Coincident(g4,g-6)
    c: Coincident(g5,g6)
    c: Coincident(g6,g7)
    c: Coincident(g5,g7)
    c: Coincident(g8,g9)
    c: Coincident(g9,g10)
    c: Coincident(g10,g8)
    c: Coincident(g11,g12)
    c: Coincident(g12,g13)
    c: Coincident(g13,g11)
    c: Coincident(g14,g15)
    c: Coincident(g15,g16)
    c: Coincident(g16,g14)
    c: Horizontal(g5,g4)
    c: Horizontal(g8,g-7)
    c: Horizontal(g11,g-8)
    c: Horizontal(g14,g-9)
    c: Coincident(g17,g5)
    c: PointOnObject(g17,g2)
    c: Perpendicular(g2,g17)
    c: Distance(g17,g17) = 3
    c: Parallel(g2,g6)
    c: Coincident(g18,g8)
    c: PointOnObject(g18,g0)
    c: Perpendicular(g18,g0)
    c: Equal(g17,g18)
    c: Parallel(g10,g0)
    c: PointOnObject(g5,g10)
    c: PointOnObject(g8,g6)
    c: PointOnObject(g11,g6)
    c: PointOnObject(g12,g6)
    c: PointOnObject(g14,g10)
    c: PointOnObject(g11,g10)
    c: PointOnObject(g14,g12)
    c: PointOnObject(g15,g10)
    c: Parallel(g7,g-6)
    c: Parallel(g8,g-6)
    c: Parallel(g9,g-7)
    c: Parallel(g11,g-7)
    c: Parallel(g13,g-8)
    c: Parallel(g14,g-8)
    c: Parallel(g15,g-9)
    c: Coincident(g19,g20)
    c: Coincident(g20,g21)
    c: Coincident(g21,g19)
    c: Coincident(g22,g23)
    c: Coincident(g23,g24)
    c: Coincident(g24,g22)
    c: Coincident(g25,g26)
    c: Coincident(g26,g27)
    c: Coincident(g27,g25)
    c: Coincident(g28,g29)
    c: Coincident(g29,g30)
    c: Coincident(g30,g28)
    c: Parallel(g24,g28)
    c: Parallel(g28,g16)
    c: Parallel(g12,g20)
    c: Parallel(g20,g26)
    c: Horizontal(g19,g-10)
    c: Horizontal(g22,g-11)
    c: Horizontal(g25,g-12)
    c: Horizontal(g29,g-13)
    c: PointOnObject(g19,g12)
    c: PointOnObject(g25,g20)
    c: PointOnObject(g22,g20)
    c: PointOnObject(g22,g16)
    c: PointOnObject(g25,g24)
    c: PointOnObject(g28,g24)
    c: PointOnObject(g29,g26)
    c: Parallel(g19,g-9)
    c: Parallel(g21,g-10)
    c: Parallel(g22,g-10)
    c: Parallel(g23,g-11)
    c: Parallel(g25,g-11)
    c: Parallel(g27,g-12)
    c: Parallel(g30,g-12)
    c: Parallel(g29,g-13)
    c: PointOnObject(g19,g16)
    c: Coincident(g31,g32)
    c: Coincident(g32,g33)
    c: Coincident(g33,g31)
    c: Coincident(g34,g35)
    c: Coincident(g35,g36)
    c: Coincident(g36,g34)
    c: Coincident(g37,g38)
    c: Coincident(g38,g39)
    c: Coincident(g39,g37)
    c: Coincident(g40,g41)
    c: Coincident(g41,g42)
    c: Coincident(g42,g40)
    c: Coincident(g43,g44)
    c: Coincident(g44,g45)
    c: Coincident(g45,g43)
    c: Parallel(g26,g32)
    c: Parallel(g32,g38)
    c: Parallel(g38,g44)
    c: Parallel(g28,g36)
    c: Parallel(g36,g40)
    c: Horizontal(g31,g-14)
    c: Horizontal(g34,g-15)
    c: Horizontal(g37,g-16)
    c: Horizontal(g41,g-17)
    c: Horizontal(g43,g-17)
    c: Parallel(g31,g-13)
    c: Parallel(g33,g-14)
    c: Parallel(g34,g-14)
    c: Parallel(g35,g-15)
    c: Parallel(g37,g-15)
    c: Parallel(g39,g-16)
    c: Parallel(g42,g-16)
    c: Parallel(g43,g-17)
    c: Parallel(g41,g-17)
    c: Parallel(g45,g-18)
    c: PointOnObject(g31,g26)
    c: PointOnObject(g31,g28)
    c: PointOnObject(g34,g28)
    c: PointOnObject(g34,g32)
    c: PointOnObject(g37,g32)
    c: PointOnObject(g37,g36)
    c: PointOnObject(g40,g36)
    c: PointOnObject(g41,g38)
    c: PointOnObject(g43,g38)
    c: PointOnObject(g43,g40)
    c: PointOnObject(g0,g-5)
    c: Horizontal(g5)
    c: PointOnObject(g0,g-18)
FEATURE [PartDesign::Pad] Pad001
  Direction = (0,0,1)
  Length = 1.2
  Length2 = 10
  Profile = -> Sketch006
  ReferenceAxis = -> Sketch006 [N_Axis]
  Refine = true
  Suppressed = false
  Type = 0
FEATURE [PartDesign::Chamfer] Chamfer001
  Angle = 50
  Base = -> Pad001 [Edge4,Edge10]
  BaseFeature = -> Pad001
  ChamferType = 2
  FlipDirection = false
  Refine = true
  Size = 1
  Size2 = 1
  SupportTransform = false
  Suppressed = false
  UseAllEdges = false
FEATURE [Sketcher::SketchObject] Sketch007
  ArcFitTolerance = 1e-06
  AttachmentSupport = -> [Chamfer001]
  ExternalGeometry = -> [Chamfer001]
  FullyConstrained = true
  MakeInternals = false
  MapMode = 5
  Placement = pos=(0,447.801,0) rot=(0,0.707107,0.707107;3.14159rad)
  sketch-geometry (4):
    g0: LineSegment StartX=-16.459 StartY=1.2 StartZ=0 EndX=-14.6712 EndY=2.7 EndZ=0
    g1: LineSegment StartX=-14.6712 StartY=2.7 StartZ=0 EndX=-0.5 EndY=2.7 EndZ=0
    g2: LineSegment StartX=-0.5 StartY=2.7 StartZ=0 EndX=-0.5 EndY=1.2 EndZ=0
    g3: LineSegment StartX=-0.5 StartY=1.2 StartZ=0 EndX=-16.459 EndY=1.2 EndZ=0
  constraints (11):
    c: Coincident(g0,g1)
    c: Horizontal(g1)
    c: Coincident(g1,g2)
    c: Coincident(g2,g3)
    c: Coincident(g3,g0)
    c: Horizontal(g3)
    c: Vertical(g2)
    c: DistanceX(g2,g-1) = 0.5
    c: Distance(g2,g2) = 1.5
    c: Parallel(g0,g-4)
    c: Coincident(g0,g-4)
FEATURE [Sketcher::SketchObject] Sketch009
  ArcFitTolerance = 1e-06
  AttachmentSupport = -> [Chamfer001]
  ExternalGeometry = -> [Chamfer001]
  FullyConstrained = true
  MakeInternals = false
  MapMode = 5
  Placement = pos=(10.1159,0.149083,12.057) rot=(-0.016985,0.999837,-0.006181;0.698146rad)
  expr: Constraints[2] = VarSet.IronSupportWidth * 2
  sketch-geometry (1):
    g0: LineSegment StartX=8.2508 StartY=449.252 StartZ=0 EndX=8.30852 EndY=446.252 EndZ=0
  constraints (3):
    c: Parallel(g0,g-3)
    c: Symmetric(g0,g0,g-3)
    c: DistanceY(g0,g0) = 3
FEATURE [PartDesign::AdditivePipe] AdditivePipe002
  AuxilleryCurvelinear = true
  AuxillerySpineTangent = false
  BaseFeature = -> Chamfer001
  Binormal = (0,0,0)
  Mode = 0
  Profile = -> Sketch007
  Refine = true
  Spine = -> Sketch009
  SpineTangent = false
  Suppressed = false
  Transformation = 0
  Transition = 0
FEATURE [Sketcher::SketchObject] Sketch010
  ArcFitTolerance = 1e-06
  AttachmentSupport = -> [AdditivePipe002]
  ExternalGeometry = -> [AdditivePipe002]
  FullyConstrained = true
  MakeInternals = false
  MapMode = 5
  Placement = pos=(0,222.632,0) rot=(1,0,0;1.5708rad)
  expr: Constraints[7] = 1.5
  sketch-geometry (4):
    g0: LineSegment StartX=-19.7774 StartY=1.2 StartZ=0 EndX=-17.9896 EndY=2.7 EndZ=0
    g1: LineSegment StartX=-17.9896 StartY=2.7 StartZ=0 EndX=-0.5 EndY=2.7 EndZ=0
    g2: LineSegment StartX=-0.5 StartY=2.7 StartZ=0 EndX=-0.5 EndY=1.2 EndZ=0
    g3: LineSegment StartX=-0.5 StartY=1.2 StartZ=0 EndX=-19.7774 EndY=1.2 EndZ=0
  constraints (11):
    c: Coincident(g0,g1)
    c: Horizontal(g1)
    c: Coincident(g1,g2)
    c: Coincident(g2,g3)
    c: Coincident(g3,g0)
    c: Horizontal(g3)
    c: Vertical(g2)
    c: Distance(g2,g2) = 1.5
    c: DistanceX(g3,g-1) = 0.5
    c: Parallel(g0,g-3)
    c: Coincident(g0,g-4)
FEATURE [Sketcher::SketchObject] Sketch011
  ArcFitTolerance = 1e-06
  AttachmentSupport = -> [AdditivePipe002]
  ExternalGeometry = -> [AdditivePipe002]
  FullyConstrained = true
  MakeInternals = false
  MapMode = 5
  Placement = pos=(-10.1159,0.149083,12.057) rot=(-0.016985,-0.999837,0.006181;0.698146rad)
  expr: Constraints[2] = VarSet.IronSupportWidth * 2
  sketch-geometry (1):
    g0: LineSegment StartX=-12.5823 StartY=224.1 StartZ=0 EndX=-12.6401 EndY=221.101 EndZ=0
  constraints (3):
    c: Parallel(g0,g-3)
    c: Symmetric(g0,g0,g-3)
    c: Distance(g0,g0) = 3
FEATURE [PartDesign::AdditivePipe] AdditivePipe003
  AuxilleryCurvelinear = true
  AuxillerySpineTangent = false
  BaseFeature = -> AdditivePipe002
  Binormal = (0,0,0)
  Mode = 0
  Profile = -> Sketch010
  Refine = true
  Spine = -> Sketch011
  SpineTangent = false
  Suppressed = false
  Transformation = 0
  Transition = 0
FEATURE [PartDesign::Mirrored] Mirrored002
  BaseFeature = -> AdditivePipe003
  MirrorPlane = -> AdditivePipe003 [Face53]
  Originals = -> [AdditivePipe003]
  Refine = true
  Suppressed = false
  TransformMode = 1
FEATURE [PartDesign::Mirrored] Mirrored003
  BaseFeature = -> Mirrored002
  MirrorPlane = -> Mirrored002 [Face59]
  Originals = -> [Mirrored002]
  Refine = true
  Suppressed = false
  TransformMode = 1
FEATURE [Sketcher::SketchObject] Sketch012
  ArcFitTolerance = 1e-06
  AttachmentSupport = -> [Mirrored003]
  ExternalGeometry = -> [Mirrored003]
  FullyConstrained = true
  MakeInternals = false
  MapMode = 5
  Placement = pos=(0,222.632,0) rot=(1,0,0;1.5708rad)
  sketch-geometry (3):
    g0: LineSegment StartX=-19.7774 StartY=1.2 StartZ=0 EndX=-17.9237 EndY=1.2 EndZ=0
    g1: LineSegment StartX=-19.7774 StartY=2.7 StartZ=0 EndX=-19.7774 EndY=1.2 EndZ=0
    g2: LineSegment StartX=-19.7774 StartY=2.7 StartZ=0 EndX=-17.9237 EndY=1.2 EndZ=0
  constraints (7):
    c: Coincident(g1,g0)
    c: Vertical(g1)
    c: Coincident(g0,g-3)
    c: Coincident(g0,g-4)
    c: DistanceY(g1,g1) = 1.5
    c: Coincident(g2,g1)
    c: Coincident(g2,g0)
FEATURE [PartDesign::AdditivePipe] AdditivePipe004
  AuxilleryCurvelinear = true
  AuxillerySpineTangent = false
  BaseFeature = -> Mirrored003
  Binormal = (0,0,0)
  Mode = 0
  Profile = -> Sketch012
  Refine = true
  Spine = -> Mirrored003 [Edge19]
  SpineTangent = false
  Suppressed = false
  Transformation = 0
  Transition = 0
FEATURE [PartDesign::Body] Body002  label="TowerMiddleSection"
  AllowCompound = true
  Group = -> [Binder001,Sketch006,Pad001,Chamfer001,Sketch007,Sketch009,AdditivePipe002,Sketch010,Sketch011,AdditivePipe003,Mirrored002,Mirrored003,Sketch012,AdditivePipe004]
  Origin = -> Origin002
  Tip = -> AdditivePipe004
FEATURE [PartDesign::SubShapeBinder] Binder002
  BindCopyOnChange = 0
  BindMode = 0
  ClaimChildren = false
  Context = -> Body003 [Binder002.]
  Fuse = false
  MakeFace = true
  OffsetFill = false
  OffsetIntersection = false
  OffsetJoinType = 0
  OffsetOpenResult = false
  PartialLoad = false
  Refine = true
  Relative = true
  Support = -> [Body[Sketch001.]]
  _Version = 2
FEATURE [Sketcher::SketchObject] Sketch013
  ArcFitTolerance = 1e-06
  AttachmentSupport = -> [XY_Plane003]
  ExternalGeometry = -> [Binder002]
  FullyConstrained = true
  MakeInternals = false
  MapMode = 5
  expr: Constraints[113] = VarSet.IronLegWidth
  expr: Constraints[20] = VarSet.IronLegWidth
  sketch-geometry (39):
    g0: LineSegment StartX=-24.2723 StartY=-1.5 StartZ=0 EndX=-20.9691 EndY=222.632 EndZ=0
    g1: LineSegment StartX=-20.9691 StartY=222.632 StartZ=0 EndX=20.9691 EndY=222.632 EndZ=0
    g2: LineSegment StartX=20.9691 StartY=222.632 StartZ=0 EndX=24.2723 EndY=-1.5 EndZ=0
    g3: LineSegment StartX=24.2723 StartY=-1.5 StartZ=0 EndX=-24.2723 EndY=-1.5 EndZ=0
    g4: LineSegment StartX=-17.9909 StartY=221.132 StartZ=0 EndX=17.9909 EndY=221.132 EndZ=0
    g5: LineSegment StartX=17.9909 StartY=221.132 StartZ=0 EndX=18.2695 EndY=202.232 EndZ=0
    g6: LineSegment StartX=18.2695 StartY=202.232 StartZ=0 EndX=-17.9909 EndY=221.132 EndZ=0
    g7: LineSegment [constr] StartX=17.9909 StartY=221.132 StartZ=0 EndX=20.9906 EndY=221.176 EndZ=0
    g8: LineSegment [constr] StartX=-20.9906 StartY=221.176 StartZ=0 EndX=-17.9909 EndY=221.132 EndZ=0
    g9: LineSegment StartX=-18.0138 StartY=219.58 StartZ=0 EndX=18.2927 EndY=200.656 EndZ=0
    g10: LineSegment StartX=18.2927 StartY=200.656 StartZ=0 EndX=-18.5759 EndY=181.439 EndZ=0
    g11: LineSegment StartX=-18.5759 StartY=181.439 StartZ=0 EndX=-18.0138 EndY=219.58 EndZ=0
    g12: LineSegment StartX=-18.5991 StartY=179.863 StartZ=0 EndX=18.3156 EndY=199.104 EndZ=0
    g13: LineSegment StartX=18.3156 StartY=199.104 StartZ=0 EndX=18.8871 EndY=160.324 EndZ=0
    g14: LineSegment StartX=18.8871 StartY=160.324 StartZ=0 EndX=-18.5991 EndY=179.863 EndZ=0
    g15: LineSegment StartX=-19.2031 StartY=138.882 StartZ=0 EndX=-18.622 EndY=178.311 EndZ=0
    g16: LineSegment StartX=-18.622 StartY=178.311 StartZ=0 EndX=18.9103 EndY=158.748 EndZ=0
    g17: LineSegment StartX=18.9103 StartY=158.748 StartZ=0 EndX=-19.2031 EndY=138.882 EndZ=0
    g18: LineSegment StartX=-19.2263 StartY=137.306 StartZ=0 EndX=18.9332 EndY=157.196 EndZ=0
    g19: LineSegment StartX=18.9332 StartY=157.196 StartZ=0 EndX=19.524 EndY=117.108 EndZ=0
    g20: LineSegment StartX=19.524 StartY=117.108 StartZ=0 EndX=-19.2263 EndY=137.306 EndZ=0
    g21: LineSegment StartX=-19.2263 StartY=137.306 StartZ=0 EndX=19.524 EndY=117.108 EndZ=0
    g22: LineSegment StartX=19.524 StartY=117.108 StartZ=0 EndX=-19.8262 EndY=96.5973 EndZ=0
    g23: LineSegment StartX=-19.8262 StartY=96.5973 StartZ=0 EndX=-19.2263 EndY=137.306 EndZ=0
    g24: LineSegment StartX=19.5701 StartY=113.98 StartZ=0 EndX=-19.8731 EndY=93.4209 EndZ=0
    g25: LineSegment StartX=-19.8731 StartY=93.4209 StartZ=0 EndX=20.1807 EndY=72.5435 EndZ=0
    g26: LineSegment StartX=20.1807 StartY=72.5435 StartZ=0 EndX=19.5701 EndY=113.98 EndZ=0
    g27: LineSegment StartX=-19.8959 StartY=91.869 StartZ=0 EndX=20.204 EndY=70.9675 EndZ=0
    g28: LineSegment StartX=20.204 StartY=70.9675 StartZ=0 EndX=-20.5168 EndY=49.7425 EndZ=0
    g29: LineSegment StartX=-20.5168 StartY=49.7425 StartZ=0 EndX=-19.8959 EndY=91.869 EndZ=0
    g30: LineSegment StartX=-20.54 StartY=48.1665 StartZ=0 EndX=20.2268 EndY=69.4156 EndZ=0
    g31: LineSegment StartX=20.2268 StartY=69.4156 StartZ=0 EndX=20.858 EndY=26.5885 EndZ=0
    g32: LineSegment StartX=20.858 StartY=26.5885 StartZ=0 EndX=-20.54 EndY=48.1665 EndZ=0
    g33: LineSegment StartX=-20.5629 StartY=46.6146 StartZ=0 EndX=20.8812 EndY=25.0125 EndZ=0
    g34: LineSegment StartX=20.8812 StartY=25.0125 StartZ=0 EndX=-21.2045 EndY=3.07598 EndZ=0
    g35: LineSegment StartX=-21.2045 StartY=3.07598 StartZ=0 EndX=-20.5629 EndY=46.6146 EndZ=0
    g36: LineSegment StartX=-21.2277 StartY=1.5 StartZ=0 EndX=20.9041 EndY=23.4605 EndZ=0
    g37: LineSegment StartX=20.9041 StartY=23.4605 StartZ=0 EndX=21.2277 EndY=1.5 EndZ=0
    g38: LineSegment StartX=21.2277 StartY=1.5 StartZ=0 EndX=-21.2277 EndY=1.5 EndZ=0
  constraints (114):
    c: Coincident(g0,g1)
    c: Coincident(g1,g2)
    c: Coincident(g2,g3)
    c: Horizontal(g3)
    c: Coincident(g0,g3)
    c: Symmetric(g0,g1,g-2)
    c: PointOnObject(g-5,g1)
    c: Parallel(g0,g-4)
    c: Horizontal(g4)
    c: Coincident(g4,g5)
    c: Coincident(g5,g6)
    c: Coincident(g6,g4)
    c: Horizontal(g4,g-6)
    c: Parallel(g5,g-3)
    c: PointOnObject(g7,g2)
    c: Symmetric(g7,g7,g-3)
    c: Coincident(g7,g4)
    c: PointOnObject(g8,g0)
    c: Coincident(g8,g4)
    c: Symmetric(g8,g4,g-4)
    c: Distance(g8,g8) = 3
    c: Parallel(g6,g-6)
    c: Coincident(g9,g10)
    c: Coincident(g10,g11)
    c: Coincident(g11,g9)
    c: Coincident(g12,g13)
    c: Coincident(g13,g14)
    c: Coincident(g14,g12)
    c: Coincident(g15,g16)
    c: Coincident(g16,g17)
    c: Coincident(g17,g15)
    c: Coincident(g18,g19)
    c: Coincident(g19,g20)
    c: Coincident(g20,g18)
    c: Parallel(g19,g13)
    c: Parallel(g13,g5)
    c: Parallel(g11,g15)
    c: Parallel(g11,g-4)
    c: PointOnObject(g4,g11)
    c: Horizontal(g9,g-7)
    c: Horizontal(g12,g-8)
    c: Horizontal(g16,g-9)
    c: Horizontal(g18,g-10)
    c: Parallel(g18,g17)
    c: Parallel(g17,g12)
    c: Parallel(g12,g10)
    c: Parallel(g10,g-7)
    c: Parallel(g14,g-8)
    c: Parallel(g-8,g16)
    c: Parallel(g16,g20)
    c: PointOnObject(g12,g11)
    c: PointOnObject(g15,g11)
    c: PointOnObject(g12,g5)
    c: PointOnObject(g16,g13)
    c: PointOnObject(g18,g13)
    c: PointOnObject(g18,g15)
    c: PointOnObject(g9,g5)
    c: Parallel(g9,g6)
    c: Coincident(g21,g22)
    c: Coincident(g22,g23)
    c: Coincident(g23,g21)
    c: Coincident(g24,g25)
    c: Coincident(g25,g26)
    c: Coincident(g26,g24)
    c: Coincident(g27,g28)
    c: Coincident(g28,g29)
    c: Coincident(g29,g27)
    c: Coincident(g30,g31)
    c: Coincident(g31,g32)
    c: Coincident(g32,g30)
    c: Coincident(g33,g34)
    c: Coincident(g34,g35)
    c: Coincident(g35,g33)
    c: Coincident(g36,g37)
    c: Coincident(g37,g38)
    c: Coincident(g38,g36)
    c: Horizontal(g21,g19)
    c: Horizontal(g24,g-12)
    c: Horizontal(g27,g-13)
    c: Horizontal(g30,g-14)
    c: Horizontal(g33,g-15)
    c: Parallel(g23,g29)
    c: Parallel(g29,g35)
    c: Parallel(g23,g15)
    c: Parallel(g19,g26)
    c: Parallel(g26,g31)
    c: Parallel(g31,g37)
    c: PointOnObject(g21,g19)
    c: PointOnObject(g24,g23)
    c: PointOnObject(g27,g26)
    c: PointOnObject(g30,g29)
    c: PointOnObject(g33,g31)
    c: PointOnObject(g36,g35)
    c: PointOnObject(g21,g15)
    c: PointOnObject(g24,g19)
    c: PointOnObject(g27,g23)
    c: PointOnObject(g33,g29)
    c: PointOnObject(g30,g26)
    c: PointOnObject(g36,g31)
    c: Parallel(g36,g-15)
    c: Parallel(g34,g36)
    c: Parallel(g33,g-14)
    c: Parallel(g-14,g32)
    c: Parallel(g30,g-13)
    c: Parallel(g28,g30)
    c: Parallel(g27,g-12)
    c: Parallel(g25,g-12)
    c: Parallel(g24,g-11)
    c: Parallel(g22,g-11)
    c: Parallel(g21,g20)
    c: Horizontal(g38)
    c: Parallel(g2,g-3)
    c: Horizontal(g36,g-15)
    c: DistanceY(g0,g36) = 3
FEATURE [PartDesign::Pad] Pad002
  Direction = (0,0,1)
  Length = 1.2
  Length2 = 10
  Profile = -> Sketch013
  ReferenceAxis = -> Sketch013 [N_Axis]
  Refine = true
  Suppressed = false
  Type = 0
FEATURE [PartDesign::Chamfer] Chamfer002
  Angle = 50
  Base = -> Pad002 [Edge4,Edge10]
  BaseFeature = -> Pad002
  ChamferType = 2
  FlipDirection = false
  Refine = true
  Size = 1
  Size2 = 1
  SupportTransform = false
  Suppressed = false
  UseAllEdges = false
FEATURE [Sketcher::SketchObject] Sketch014
  ArcFitTolerance = 1e-06
  AttachmentSupport = -> [Chamfer002]
  ExternalGeometry = -> [Chamfer002]
  FullyConstrained = true
  MakeInternals = false
  MapMode = 5
  Placement = pos=(0,222.632,0) rot=(0,0.707107,0.707107;3.14159rad)
  sketch-geometry (4):
    g0: LineSegment StartX=-19.7773 StartY=1.2 StartZ=0 EndX=-17.9894 EndY=2.7 EndZ=0
    g1: LineSegment StartX=-17.9894 StartY=2.7 StartZ=0 EndX=-0.5 EndY=2.7 EndZ=0
    g2: LineSegment StartX=-0.5 StartY=2.7 StartZ=0 EndX=-0.5 EndY=1.2 EndZ=0
    g3: LineSegment StartX=-0.5 StartY=1.2 StartZ=0 EndX=-19.7773 EndY=1.2 EndZ=0
  constraints (11):
    c: Coincident(g0,g1)
    c: Horizontal(g1)
    c: Coincident(g1,g2)
    c: Coincident(g2,g3)
    c: Coincident(g3,g0)
    c: Horizontal(g3)
    c: Parallel(g0,g-3)
    c: DistanceX(g2,g-1) = 0.5
    c: Vertical(g2)
    c: DistanceY(g2,g2) = 1.5
    c: Coincident(g0,g-3)
FEATURE [Sketcher::SketchObject] Sketch015
  ArcFitTolerance = 1e-06
  AttachmentSupport = -> [Chamfer002]
  ExternalGeometry = -> [Chamfer002]
  FullyConstrained = true
  MakeInternals = false
  MapMode = 5
  Placement = pos=(10.1159,0.149082,12.0569) rot=(-0.016985,0.999837,-0.006181;0.698146rad)
  sketch-geometry (1):
    g0: LineSegment StartX=12.5822 StartY=224.1 StartZ=0 EndX=12.6399 EndY=221.1 EndZ=0
  constraints (3):
    c: Parallel(g0,g-3)
    c: DistanceY(g0,g0) = 3
    c: Symmetric(g0,g0,g-3)
FEATURE [PartDesign::AdditivePipe] AdditivePipe005
  AuxilleryCurvelinear = true
  AuxillerySpineTangent = false
  BaseFeature = -> Chamfer002
  Binormal = (0,0,0)
  Mode = 0
  Profile = -> Sketch014
  Refine = true
  Spine = -> Sketch015
  SpineTangent = false
  Suppressed = false
  Transformation = 0
  Transition = 0
FEATURE [PartDesign::Body] Body003
  AllowCompound = true
  Group = -> [Binder002,Sketch013,Pad002,Chamfer002,Sketch014,Sketch015,AdditivePipe005]
  Origin = -> Origin003
  Tip = -> AdditivePipe005
